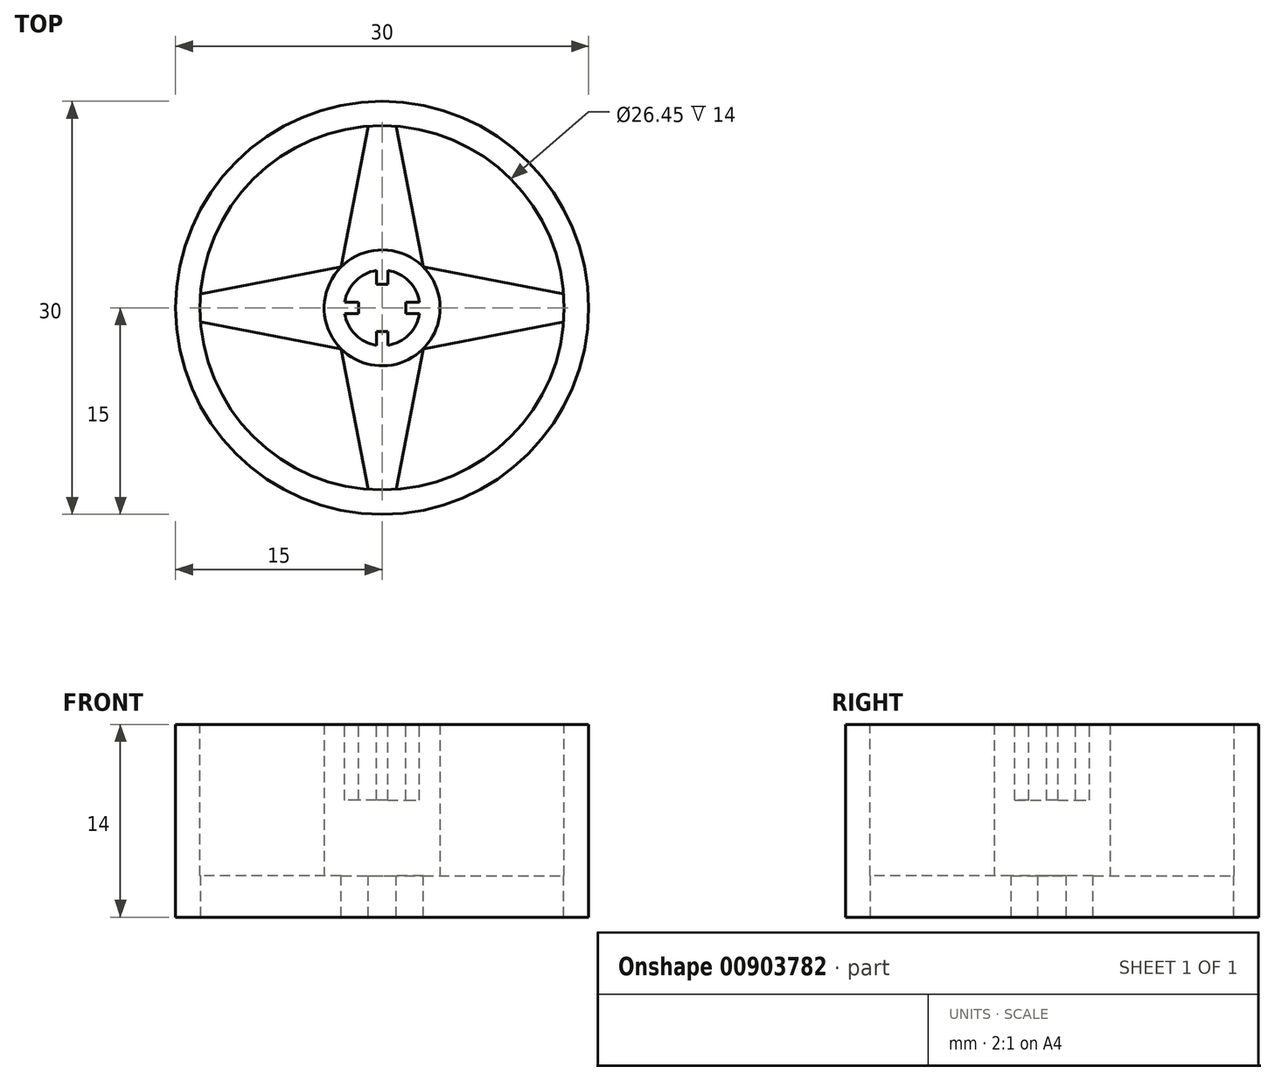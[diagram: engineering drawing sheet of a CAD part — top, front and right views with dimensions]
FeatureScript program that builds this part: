
annotation { "Feature Type Name" : "Feature", "Feature Type Description" : "" }
export const myFeature = defineFeature(function(context is Context, id is Id, definition is map)
    precondition{}
    {
        {
            var Q0;
            Q0=qCreatedBy(makeId("Top.planeOp"),FACE);
            var sketch = newSketch(context, id + "F0", { "sketchPlane" : qUnion([Q0])});
            skCircle(sketch, "E0", {"center": v(0, 0) * mm, "radius": 15 * mm});
            skSolve(sketch);
        }
        {
            var Q0;
            Q0=makeQuery(id+"F0.imprint","IMPRINT",FACE,{"disambiguationData":[TD([[makeQuery(id+"F0.imprint","IMPRINT",EDGE,{"derivedFrom":sQuery(id+"F0.wireOp",EDGE,"E0")}),1.0]])]});
            extrude(context, id + "F1", {"entities" : qUnion([Q0]), "depth" : 14 * mm, "offsetDistance" : 25 * mm});
        }
        {
            var Q0;
            Q0=makeQuery(id+"F1.opExtrude","CAP_FACE",FACE,{"disambiguationData":[OSD([sQuery(id+"F0.wireOp",EDGE,"E0")])],"isStart":false});
            var sketch = newSketch(context, id + "F2", { "sketchPlane" : qUnion([Q0])});
            skCircle(sketch, "E1", {"center": v(0, 0) * mm, "radius": 13.23 * mm});
            skSolve(sketch);
        }
        {
            var Q0;
            Q0=makeQuery(id+"F2.imprint","IMPRINT",FACE,{"disambiguationData":[TD([[makeQuery(id+"F2.imprint","IMPRINT",EDGE,{"derivedFrom":sQuery(id+"F2.wireOp",EDGE,"E1")}),1.0]])]});
            extrude(context, id + "F3", {"entities" : qUnion([Q0]), "operationType" : NewBodyOperationType.REMOVE, "oppositeDirection" : true, "depth" : 11 * mm, "offsetDistance" : 25 * mm});
        }
        {
            var Q0;
            Q0=makeQuery(id+"F3.boolean.opBoolean","COPY",FACE,{"derivedFrom":makeQuery(id+"F3.opExtrude","CAP_FACE",FACE,{"disambiguationData":[OSD([sQuery(id+"F2.wireOp",EDGE,"E1")])],"isStart":false})});
            var sketch = newSketch(context, id + "F4", { "sketchPlane" : qUnion([Q0])});
            skCircle(sketch, "E2", {"center": v(0, 0) * mm, "radius": 4.2 * mm});
            skSolve(sketch);
        }
        {
            var Q0;
            Q0=makeQuery(id+"F4.imprint","IMPRINT",FACE,{"disambiguationData":[TD([[makeQuery(id+"F4.imprint","IMPRINT",EDGE,{"derivedFrom":sQuery(id+"F4.wireOp",EDGE,"E2")}),1.0]])]});
            extrude(context, id + "F5", {"entities" : qUnion([Q0]), "operationType" : NewBodyOperationType.ADD, "depth" : 11 * mm, "offsetDistance" : 25 * mm});
        }
        {
            var Q0;
            Q0=makeQuery(id+"F5.opExtrude","CAP_FACE",FACE,{"disambiguationData":[OSD([sQuery(id+"F4.wireOp",EDGE,"E2")])],"isStart":false});
            var sketch = newSketch(context, id + "F6", { "sketchPlane" : qUnion([Q0])});
            skLineSegment(sketch, "E3", {"start": v(0, 1.7) * mm, "end": v(0.4, 1.7) * mm});
            skLineSegment(sketch, "E4", {"start": v(0.4, 1.7) * mm, "end": v(0.4, 2.72) * mm});
            skLineSegment(sketch, "E5.MirrorCS", {"start": v(-0.4, 1.7) * mm, "end": v(-0.4, 2.72) * mm});
            skLineSegment(sketch, "E6.MirrorCS", {"start": v(0, 1.7) * mm, "end": v(-0.4, 1.7) * mm});
            skLineSegment(sketch, "E7.MirrorCS", {"start": v(-0.4, -1.7) * mm, "end": v(-0.4, -2.72) * mm});
            skLineSegment(sketch, "E8.MirrorCS", {"start": v(0, -1.7) * mm, "end": v(-0.4, -1.7) * mm});
            skLineSegment(sketch, "E9.MirrorCS", {"start": v(0.4, -1.7) * mm, "end": v(0.4, -2.72) * mm});
            skLineSegment(sketch, "E10.MirrorCS", {"start": v(0, -1.7) * mm, "end": v(0.4, -1.7) * mm});
            skLineSegment(sketch, "E11.MirrorCS", {"start": v(1.7, 0) * mm, "end": v(1.7, -0.4) * mm});
            skLineSegment(sketch, "E12.MirrorCS", {"start": v(1.7, -0.4) * mm, "end": v(2.72, -0.4) * mm});
            skLineSegment(sketch, "E13.MirrorCS", {"start": v(1.7, 0.4) * mm, "end": v(2.72, 0.4) * mm});
            skLineSegment(sketch, "E14.MirrorCS", {"start": v(1.7, 0) * mm, "end": v(1.7, 0.4) * mm});
            skLineSegment(sketch, "E15.MirrorCS", {"start": v(-1.7, -0.4) * mm, "end": v(-2.72, -0.4) * mm});
            skLineSegment(sketch, "E16.MirrorCS", {"start": v(-1.7, 0) * mm, "end": v(-1.7, -0.4) * mm});
            skLineSegment(sketch, "E17.MirrorCS", {"start": v(-1.7, 0.4) * mm, "end": v(-2.72, 0.4) * mm});
            skLineSegment(sketch, "E18.MirrorCS", {"start": v(-1.7, 0) * mm, "end": v(-1.7, 0.4) * mm});
            skArc(sketch, "E19", {"start": v(-0.4, 2.72) * mm, "mid": v(-1.94, 1.94) * mm, "end": v(-2.72, 0.4) * mm});
            skArc(sketch, "E20", {"start": v(-2.72, -0.4) * mm, "mid": v(-1.94, -1.94) * mm, "end": v(-0.4, -2.72) * mm});
            skArc(sketch, "E21", {"start": v(0.4, -2.72) * mm, "mid": v(1.94, -1.94) * mm, "end": v(2.72, -0.4) * mm});
            skArc(sketch, "E22", {"start": v(2.72, 0.4) * mm, "mid": v(1.94, 1.94) * mm, "end": v(0.4, 2.72) * mm});
            skSolve(sketch);
        }
        {
            var Q0;
            Q0=makeQuery(id+"F6.imprint","IMPRINT",FACE,{"disambiguationData":[TD([[makeQuery(id+"F6.imprint","IMPRINT",EDGE,{"derivedFrom":sQuery(id+"F6.wireOp",EDGE,"E3")}),-1.0]])]});
            extrude(context, id + "F7", {"entities" : qUnion([Q0]), "operationType" : NewBodyOperationType.REMOVE, "oppositeDirection" : true, "depth" : 5.5 * mm, "offsetDistance" : 25 * mm});
        }
        {
            var Q0;
            Q0=makeQuery(id+"F3.boolean.opBoolean","COPY",FACE,{"derivedFrom":makeQuery(id+"F3.opExtrude","CAP_FACE",FACE,{"disambiguationData":[OSD([sQuery(id+"F2.wireOp",EDGE,"E1")])],"isStart":false})});
            var sketch = newSketch(context, id + "F8", { "sketchPlane" : qUnion([Q0])});
            skLineSegment(sketch, "E23", {"start": v(2.98, 2.98) * mm, "end": v(1.03, 13.19) * mm});
            skLineSegment(sketch, "E24.MirrorCS", {"start": v(-2.98, 2.98) * mm, "end": v(-1.03, 13.19) * mm});
            skLineSegment(sketch, "E25.MirrorCS", {"start": v(2.98, -2.98) * mm, "end": v(1.03, -13.19) * mm});
            skLineSegment(sketch, "E26.MirrorCS", {"start": v(-2.98, -2.98) * mm, "end": v(-1.03, -13.19) * mm});
            skLineSegment(sketch, "E27.MirrorCS", {"start": v(2.98, 2.98) * mm, "end": v(13.19, 1.03) * mm});
            skLineSegment(sketch, "E28.MirrorCS", {"start": v(2.98, -2.98) * mm, "end": v(13.19, -1.03) * mm});
            skLineSegment(sketch, "E29.MirrorCS", {"start": v(-2.98, -2.98) * mm, "end": v(-13.19, -1.03) * mm});
            skLineSegment(sketch, "E30.MirrorCS", {"start": v(-2.98, 2.98) * mm, "end": v(-13.19, 1.03) * mm});
            skArc(sketch, "E31", {"start": v(-13.19, 1.03) * mm, "mid": v(-9.35, 9.35) * mm, "end": v(-1.03, 13.19) * mm});
            skArc(sketch, "E32", {"start": v(1.03, 13.19) * mm, "mid": v(9.35, 9.35) * mm, "end": v(13.19, 1.03) * mm});
            skArc(sketch, "E33", {"start": v(13.19, -1.03) * mm, "mid": v(9.35, -9.35) * mm, "end": v(1.03, -13.19) * mm});
            skArc(sketch, "E34", {"start": v(-1.03, -13.19) * mm, "mid": v(-9.35, -9.35) * mm, "end": v(-13.19, -1.03) * mm});
            skSolve(sketch);
        }
        {
            var Q0;
            Q0 = qSketchRegion(id + "F8", true);
            extrude(context, id + "F9", {"entities" : qUnion([Q0]), "operationType" : NewBodyOperationType.REMOVE, "endBound" : BoundingType.UP_TO_NEXT, "oppositeDirection" : true, "depth" : 25 * mm, "offsetDistance" : 25 * mm});
        }
    });
